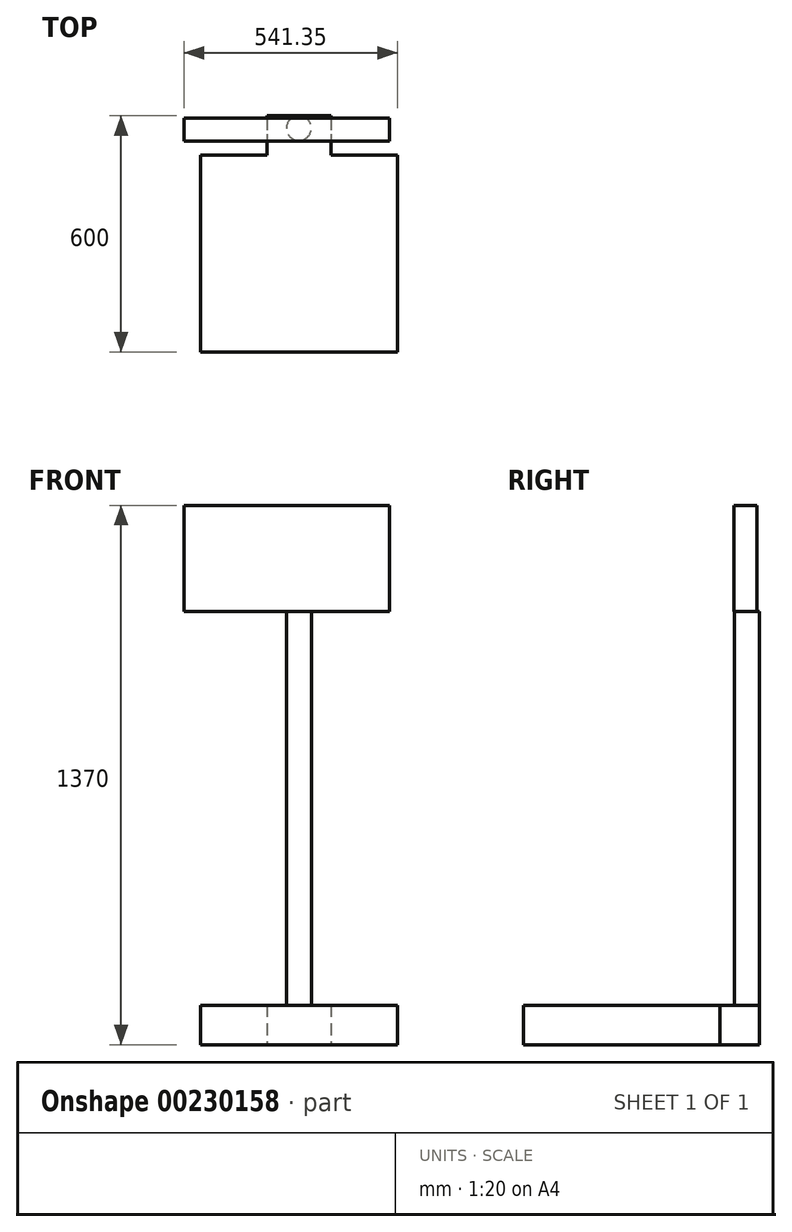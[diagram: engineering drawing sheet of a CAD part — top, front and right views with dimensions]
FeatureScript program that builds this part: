
annotation { "Feature Type Name" : "Feature", "Feature Type Description" : "" }
export const myFeature = defineFeature(function(context is Context, id is Id, definition is map)
    precondition{}
    {
        {
            var Q0;
            Q0=qCreatedBy(makeId("Top.planeOp"),FACE);
            var sketch = newSketch(context, id + "F0", { "sketchPlane" : qUnion([Q0])});
            skLineSegment(sketch, "E0.bottom", {"start": v(250, 250) * mm, "end": v(-250, 250) * mm});
            skLineSegment(sketch, "E0.top", {"start": v(250, -250) * mm, "end": v(-250, -250) * mm});
            skLineSegment(sketch, "E0.left", {"start": v(250, 250) * mm, "end": v(250, -250) * mm});
            skLineSegment(sketch, "E0.right", {"start": v(-250, 250) * mm, "end": v(-250, -250) * mm});
            skPoint(sketch, "E0.middle", {"position": v(0, 0) * mm});
            skSolve(sketch);
        }
        {
            var Q0;
            Q0 = qSketchRegion(id + "F0", true);
            extrude(context, id + "F1", {"entities" : qUnion([Q0]), "depth" : 100 * mm});
        }
        {
            var Q0;
            Q0=makeQuery(id+"F1.opExtrude","SWEPT_FACE",FACE,{"disambiguationData":[OSD([sQuery(id+"F0.wireOp",EDGE,"E0.bottom")])]});
            var sketch = newSketch(context, id + "F2", { "sketchPlane" : qUnion([Q0])});
            skLineSegment(sketch, "E1.bottom", {"start": v(81.3, 100) * mm, "end": v(-81.3, 100) * mm});
            skLineSegment(sketch, "E1.top", {"start": v(81.3, 0) * mm, "end": v(-81.3, 0) * mm});
            skLineSegment(sketch, "E1.left", {"start": v(81.3, 100) * mm, "end": v(81.3, 0) * mm});
            skLineSegment(sketch, "E1.right", {"start": v(-81.3, 100) * mm, "end": v(-81.3, 0) * mm});
            skPoint(sketch, "E1.middle", {"position": v(0, 50) * mm});
            skPoint(sketch, "E1.middle.positionSnap0", {"position": v(0, 0) * mm});
            skPoint(sketch, "E1.middle.positionSnap1", {"position": v(250, 50) * mm});
            skPoint(sketch, "E1.centerSnap0", {"position": v(0, 0) * mm});
            skPoint(sketch, "E1.centerSnap1", {"position": v(250, 50) * mm});
            skSolve(sketch);
        }
        {
            var Q0;
            Q0 = qSketchRegion(id + "F2", true);
            extrude(context, id + "F3", {"entities" : qUnion([Q0]), "operationType" : NewBodyOperationType.ADD, "depth" : 100 * mm});
        }
        {
            var Q0;
            Q0=makeQuery(id+"F3.boolean.opBoolean","MERGE",FACE,{"derivedFrom":[makeQuery(id+"F1.opExtrude","CAP_FACE",FACE,{"disambiguationData":[OSD([sQuery(id+"F0.wireOp",EDGE,"E0.bottom"),sQuery(id+"F0.wireOp",EDGE,"E0.top"),sQuery(id+"F0.wireOp",EDGE,"E0.left"),sQuery(id+"F0.wireOp",EDGE,"E0.right")])],"isStart":false}),makeQuery(id+"F3.opExtrude","SWEPT_FACE",FACE,{"disambiguationData":[OSD([sQuery(id+"F2.wireOp",EDGE,"E1.bottom")])]})]});
            var sketch = newSketch(context, id + "F4", { "sketchPlane" : qUnion([Q0])});
            skCircle(sketch, "E2", {"center": v(0, 318.5) * mm, "radius": 31.5 * mm});
            skSolve(sketch);
        }
        {
            var Q0;
            Q0 = qSketchRegion(id + "F4", true);
            extrude(context, id + "F5", {"entities" : qUnion([Q0]), "operationType" : NewBodyOperationType.ADD, "offsetDistance" : 25 * mm, "depth" : 1000 * mm});
        }
        {
            var Q0;
            Q0=makeQuery(id+"F5.opExtrude","CAP_FACE",FACE,{"disambiguationData":[OSD([sQuery(id+"F4.wireOp",EDGE,"E2")])],"isStart":false});
            var sketch = newSketch(context, id + "F6", { "sketchPlane" : qUnion([Q0])});
            skLineSegment(sketch, "E3.bottom", {"start": v(146.35, 285.4) * mm, "end": v(-146.35, 285.4) * mm});
            skLineSegment(sketch, "E3.top", {"start": v(146.35, 343.48) * mm, "end": v(-146.35, 343.48) * mm});
            skLineSegment(sketch, "E3.left", {"start": v(146.35, 285.4) * mm, "end": v(146.35, 343.48) * mm});
            skLineSegment(sketch, "E3.right", {"start": v(-146.35, 285.4) * mm, "end": v(-146.35, 343.48) * mm});
            skPoint(sketch, "E3.middle", {"position": v(0, 314.43) * mm});
            skSolve(sketch);
        }
        {
            var Q0;
            Q0 = qSketchRegion(id + "F6", true);
            extrude(context, id + "F7", {"entities" : qUnion([Q0]), "operationType" : NewBodyOperationType.ADD, "depth" : 270 * mm});
        }
        {
            var Q0;
            Q0=makeQuery(id+"F7.opExtrude","SWEPT_FACE",FACE,{"disambiguationData":[OSD([sQuery(id+"F6.wireOp",EDGE,"E3.right")])]});
            extrude(context, id + "F8", {"entities" : qUnion([Q0]), "operationType" : NewBodyOperationType.ADD, "depth" : 145 * mm});
        }
        {
            var Q0;
            Q0=makeQuery(id+"F7.opExtrude","SWEPT_FACE",FACE,{"disambiguationData":[OSD([sQuery(id+"F6.wireOp",EDGE,"E3.left")])]});
            extrude(context, id + "F9", {"entities" : qUnion([Q0]), "operationType" : NewBodyOperationType.ADD, "depth" : 84 * mm});
        }
    });
